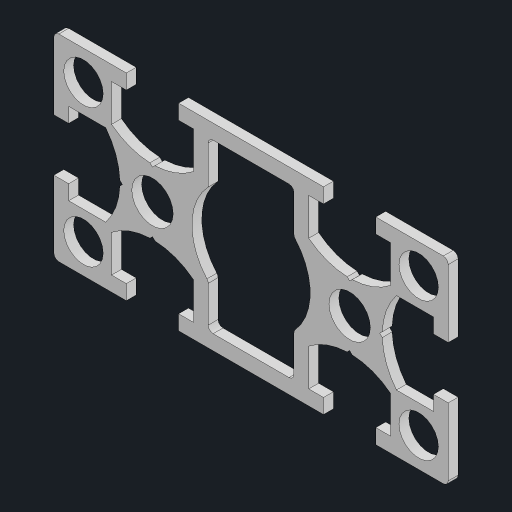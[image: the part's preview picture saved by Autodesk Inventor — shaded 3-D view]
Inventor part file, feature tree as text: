
AUTODESK INVENTOR PART (.ipt)
format: ipt  version: 2024.1 (Build 281209000, 209)  size: 323,072 bytes
history: native  units: mm
features: other x1, extrude x1, sketch x1
ambient origin geometry x8: Origin, YZ Plane, XZ Plane, XY Plane, X Axis, Y Axis, Z Axis, Center Point
bodies: Body1 (feature_tree)
feature tree (3):
  other  "솔리드1"
  extrude  "돌출1"  Depth=40.0mm
  sketch  "스케치1"
